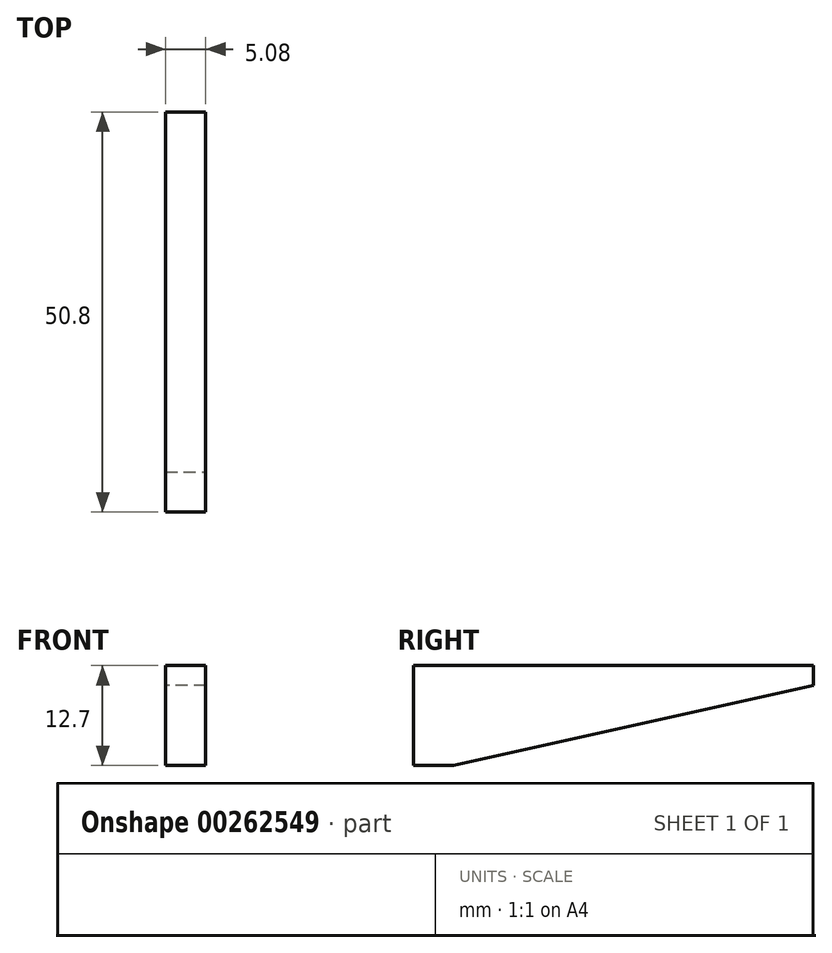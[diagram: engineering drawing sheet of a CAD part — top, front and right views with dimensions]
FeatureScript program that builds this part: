
annotation { "Feature Type Name" : "Feature", "Feature Type Description" : "" }
export const myFeature = defineFeature(function(context is Context, id is Id, definition is map)
    precondition{}
    {
        {
            var Q0;
            Q0=qCreatedBy(makeId("Front.planeOp"),FACE);
            var sketch = newSketch(context, id + "F0", { "sketchPlane" : qUnion([Q0])});
            skLineSegment(sketch, "E0.bottom", {"start": v(2.54, 6.35) * mm, "end": v(-2.54, 6.35) * mm});
            skLineSegment(sketch, "E0.top", {"start": v(2.54, -6.35) * mm, "end": v(-2.54, -6.35) * mm});
            skLineSegment(sketch, "E0.left", {"start": v(2.54, 6.35) * mm, "end": v(2.54, -6.35) * mm});
            skLineSegment(sketch, "E0.right", {"start": v(-2.54, 6.35) * mm, "end": v(-2.54, -6.35) * mm});
            skPoint(sketch, "E0.middle", {"position": v(0, 0) * mm});
            skSolve(sketch);
        }
        {
            var Q0;
            Q0=makeQuery(id+"F0.imprint","IMPRINT",FACE,{"disambiguationData":[TD([[makeQuery(id+"F0.imprint","IMPRINT",EDGE,{"derivedFrom":sQuery(id+"F0.wireOp",EDGE,"E0.bottom")}),1.0]])]});
            extrude(context, id + "F1", {"entities" : qUnion([Q0]), "depth" : 50.8 * mm});
        }
        {
            var Q0;
            Q0=makeQuery(id+"F1.opExtrude","CAP_EDGE",EDGE,{"disambiguationData":[OSD([sQuery(id+"F0.wireOp",EDGE,"E0.top")])],"isStart":true});
            chamfer(context, id + "F2", {"entities" : qUnion([Q0]), "chamferType" : ChamferType.TWO_OFFSETS, "width1" : 10.16 * mm, "oppositeDirection" : false, "width2" : 45.72 * mm, "tangentPropagation" : true});
        }
    });
